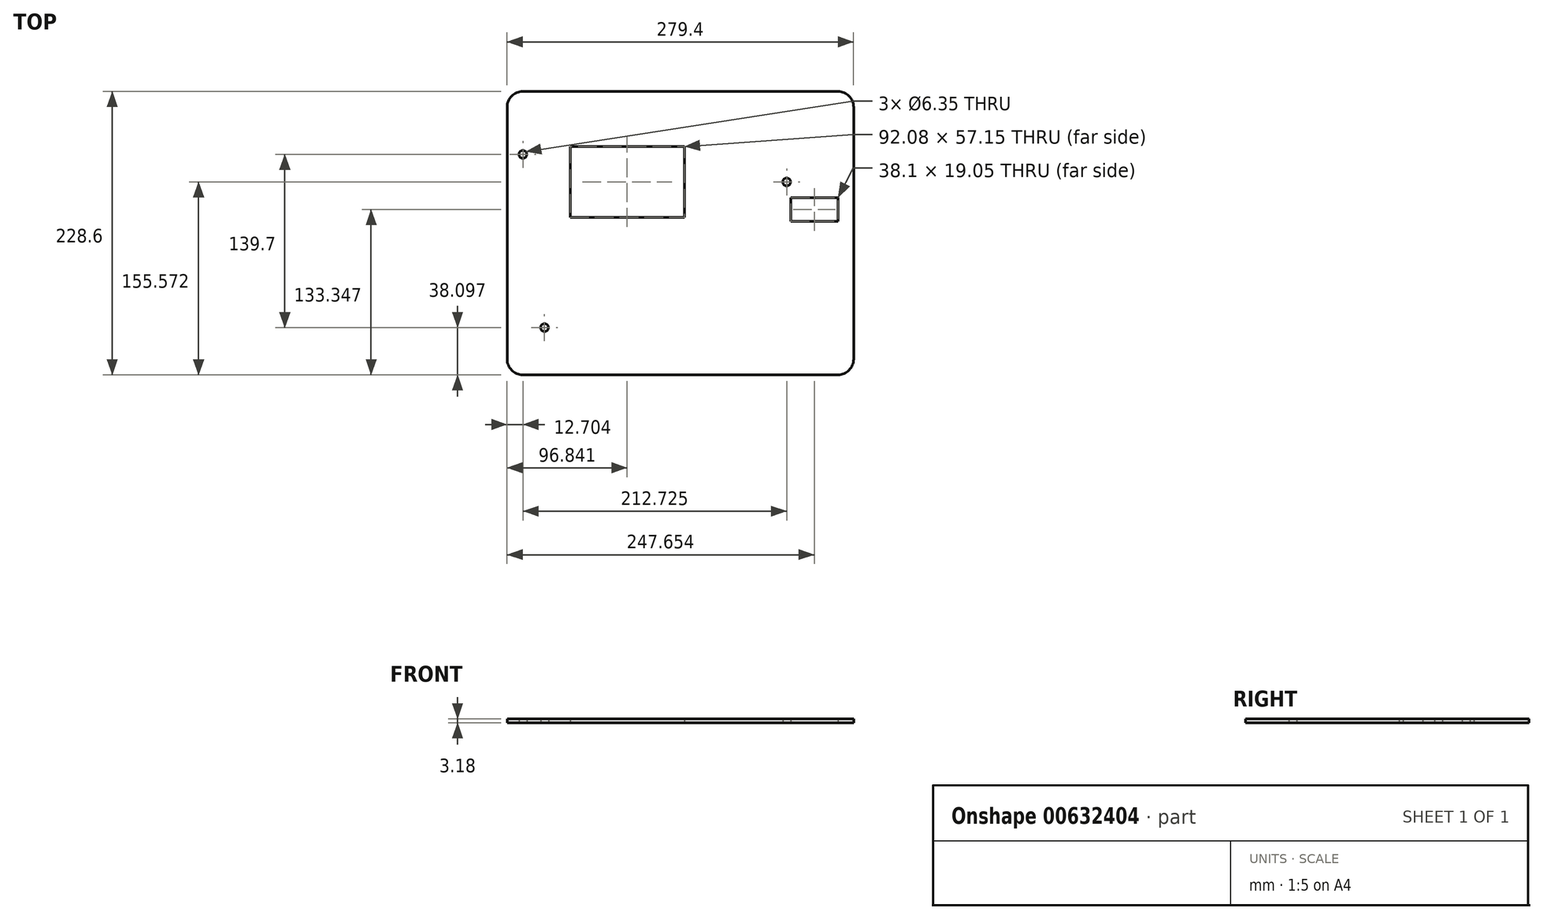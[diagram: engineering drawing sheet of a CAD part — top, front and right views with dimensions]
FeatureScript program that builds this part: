
annotation { "Feature Type Name" : "Feature", "Feature Type Description" : "" }
export const myFeature = defineFeature(function(context is Context, id is Id, definition is map)
    precondition{}
    {
        {
            var Q0;
            Q0=qCreatedBy(makeId("Top.planeOp"),FACE);
            var sketch = newSketch(context, id + "F0", { "sketchPlane" : qUnion([Q0])});
            skLineSegment(sketch, "E0.bottom", {"start": v(-123.63, 129.7) * mm, "end": v(130.37, 129.7) * mm});
            skLineSegment(sketch, "E0.top", {"start": v(-123.63, -98.9) * mm, "end": v(130.37, -98.9) * mm});
            skLineSegment(sketch, "E0.left", {"start": v(-136.33, 117) * mm, "end": v(-136.33, -86.2) * mm});
            skLineSegment(sketch, "E0.right", {"start": v(143.07, 117) * mm, "end": v(143.07, -86.2) * mm});
            skCircle(sketch, "E1", {"center": v(-123.63, 78.9) * mm, "radius": 3.18 * mm});
            skCircle(sketch, "E2", {"center": v(89.1, 56.68) * mm, "radius": 3.18 * mm});
            skCircle(sketch, "E3", {"center": v(-106.16, -60.8) * mm, "radius": 3.18 * mm});
            skLineSegment(sketch, "E4.bottom", {"start": v(-85.53, 85.26) * mm, "end": v(6.55, 85.26) * mm});
            skLineSegment(sketch, "E4.top", {"start": v(-85.53, 28.1) * mm, "end": v(6.55, 28.1) * mm});
            skLineSegment(sketch, "E4.left", {"start": v(-85.53, 85.26) * mm, "end": v(-85.53, 28.1) * mm});
            skLineSegment(sketch, "E4.right", {"start": v(6.55, 85.26) * mm, "end": v(6.55, 28.1) * mm});
            skLineSegment(sketch, "E5.bottom", {"start": v(92.27, 43.98) * mm, "end": v(130.37, 43.98) * mm});
            skLineSegment(sketch, "E5.top", {"start": v(92.27, 24.93) * mm, "end": v(130.37, 24.93) * mm});
            skLineSegment(sketch, "E5.left", {"start": v(92.27, 43.98) * mm, "end": v(92.27, 24.93) * mm});
            skLineSegment(sketch, "E5.right", {"start": v(130.37, 43.98) * mm, "end": v(130.37, 24.93) * mm});
            skPoint(sketch, "E6.visualSharp", {"position": v(-136.33, 129.7) * mm});
            skArc(sketch, "E6.filletArc", {"start": v(-123.63, 129.7) * mm, "mid": v(-132.6, 125.99) * mm, "end": v(-136.33, 117) * mm});
            skPoint(sketch, "E7.visualSharp", {"position": v(-136.33, -98.9) * mm});
            skArc(sketch, "E7.filletArc", {"start": v(-136.33, -86.2) * mm, "mid": v(-132.6, -95.17) * mm, "end": v(-123.63, -98.9) * mm});
            skPoint(sketch, "E8.visualSharp", {"position": v(143.07, -98.9) * mm});
            skArc(sketch, "E8.filletArc", {"start": v(130.37, -98.9) * mm, "mid": v(139.35, -95.17) * mm, "end": v(143.07, -86.2) * mm});
            skPoint(sketch, "E9.visualSharp", {"position": v(143.07, 129.7) * mm});
            skArc(sketch, "E9.filletArc", {"start": v(143.07, 117) * mm, "mid": v(139.35, 125.99) * mm, "end": v(130.37, 129.7) * mm});
            skSolve(sketch);
        }
        {
            var Q0;
            Q0=makeQuery(id+"F0.imprint","IMPRINT",FACE,{"disambiguationData":[TD([[makeQuery(id+"F0.imprint","IMPRINT",EDGE,{"derivedFrom":sQuery(id+"F0.wireOp",EDGE,"E0.bottom")}),-1.0]])]});
            extrude(context, id + "F1", {"entities" : qUnion([Q0]), "depth" : 3.17 * mm, "offsetDistance" : 25.4 * mm});
        }
    });
